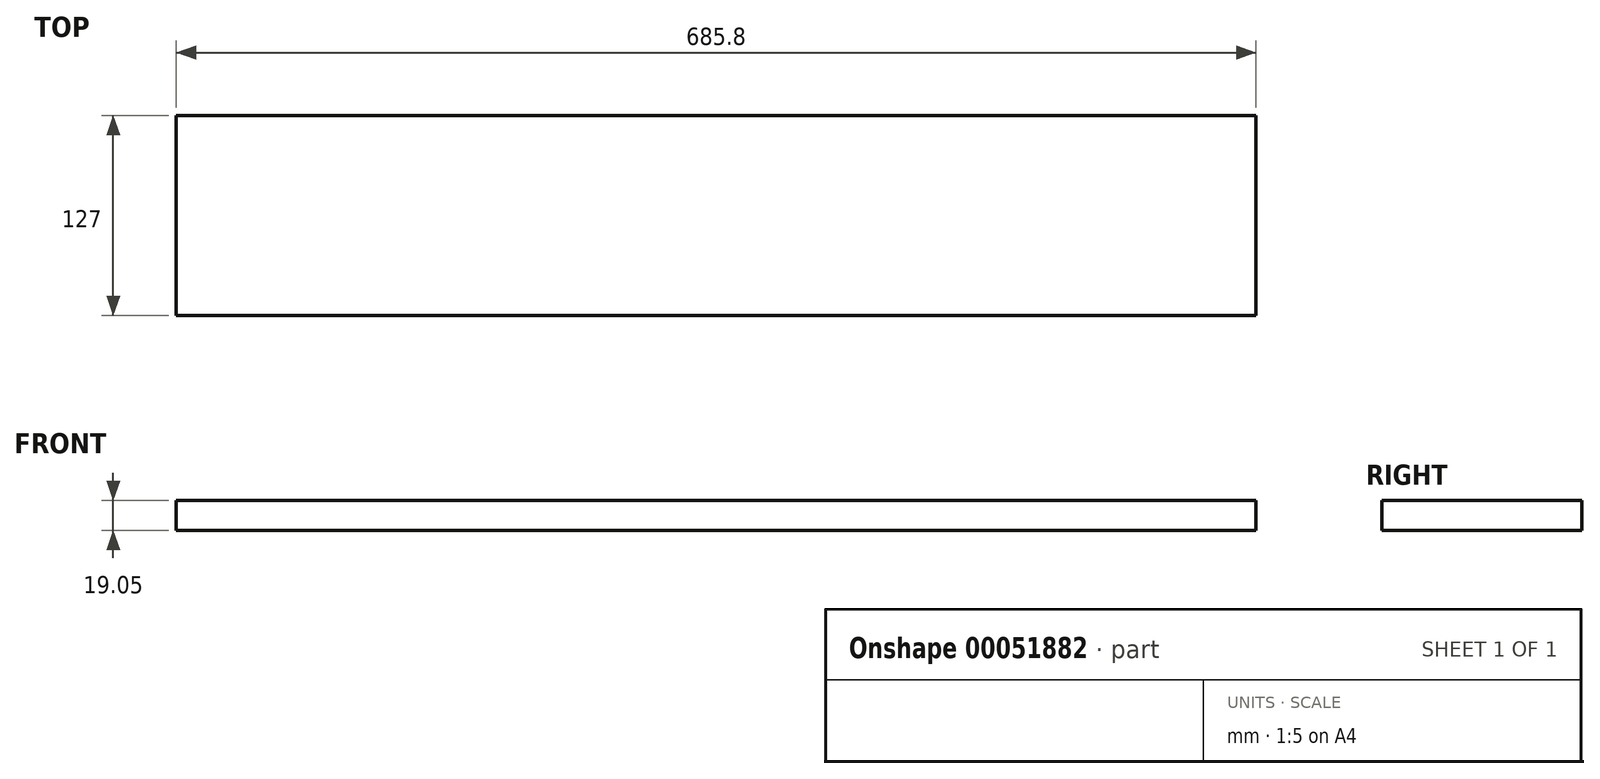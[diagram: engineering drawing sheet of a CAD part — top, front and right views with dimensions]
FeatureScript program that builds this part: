
annotation { "Feature Type Name" : "Feature", "Feature Type Description" : "" }
export const myFeature = defineFeature(function(context is Context, id is Id, definition is map)
    precondition{}
    {
        {
            var Q0;
            Q0=qCreatedBy(makeId("Top.planeOp"),FACE);
            var sketch = newSketch(context, id + "F0", { "sketchPlane" : qUnion([Q0])});
            skLineSegment(sketch, "E0.bottom", {"start": v(-342.9, 57.15) * mm, "end": v(342.9, 57.15) * mm});
            skLineSegment(sketch, "E0.top", {"start": v(-342.9, -69.85) * mm, "end": v(342.9, -69.85) * mm});
            skLineSegment(sketch, "E0.left", {"start": v(-342.9, 57.15) * mm, "end": v(-342.9, -69.85) * mm});
            skLineSegment(sketch, "E0.right", {"start": v(342.9, 57.15) * mm, "end": v(342.9, -69.85) * mm});
            skSolve(sketch);
        }
        {
            var Q0;
            Q0=makeQuery(id+"F0.imprint","IMPRINT",FACE,{"disambiguationData":[TD([[makeQuery(id+"F0.imprint","IMPRINT",EDGE,{"derivedFrom":sQuery(id+"F0.wireOp",EDGE,"E0.bottom")}),-1.0]])]});
            extrude(context, id + "F1", {"entities" : qUnion([Q0]), "depth" : 19.05 * mm});
        }
    });
